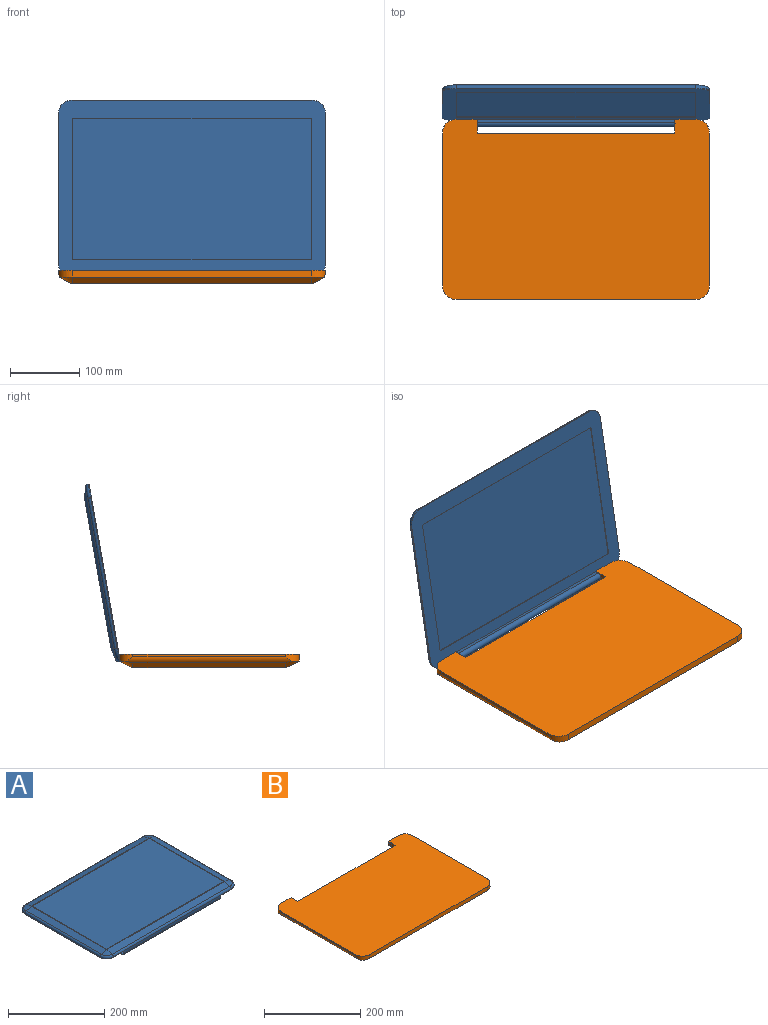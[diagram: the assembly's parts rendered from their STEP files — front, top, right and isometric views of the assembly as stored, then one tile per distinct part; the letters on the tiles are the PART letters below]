
ASSEMBLY  parts=2 mates=1
PART A: 44 faces, bbox 388.3x263.3x20.2 mm
  f0: plane 385x260mm, normal (0,0,-1), area 25707.1mm2, adj f1,f2,f3,f4,f5,f6,f7,f8
  f1: plane 220x1.1mm, normal (1,0,0), area 241.1mm2, adj f0,f2,f8,f22
  f2: cylinder r=20mm len=20mm, axis (0,0,-1), area 34.4mm2, adj f0,f1,f3,f24
  f3: plane 345x1.1mm, normal (0,1,0), area 378.2mm2, adj f0,f2,f4,f25
  f4: cylinder r=20mm len=20mm, axis (0,0,-1), area 34.4mm2, adj f0,f3,f5,f23
  f5: plane 220x1.1mm, normal (-1,0,0), area 241.1mm2, adj f0,f4,f6,f21
  f6: cylinder r=20mm len=20mm, axis (0,0,-1), area 34.4mm2, adj f0,f5,f7,f19
  f7: plane 345x6.3mm, normal (0,-1,0), area 1860.2mm2, adj f0,f6,f8,f18,f39,f41,f42
  f8: cylinder r=20mm len=20mm, axis (0,0,-1), area 34.4mm2, adj f0,f1,f7,f20
  f9: plane 343.77x218.77mm, normal (0,0,1), area 75206mm2, adj f27,f28,f31,f32
  f10: cone r=20mm half-angle=76deg, axis (0,0,-1), area 212.5mm2, adj f11,f12,f24,f26
  f11: plane 345x15.62mm, normal (0,0.24,0.97), area 5553.2mm2, adj f10,f13,f25,f27
  f12: plane 220x15.62mm, normal (0.24,0,0.97), area 3541.1mm2, adj f10,f14,f22,f28
  f13: cone r=20mm half-angle=76deg, axis (0,0,-1), area 212.5mm2, adj f11,f15,f23,f29
  f14: cone r=20mm half-angle=76deg, axis (0,0,-1), area 212.5mm2, adj f12,f16,f20,f30
  f15: plane 220x15.62mm, normal (-0.24,0,0.97), area 3541.1mm2, adj f13,f17,f21,f31
  f16: plane 345x15.62mm, normal (0,-0.24,0.97), area 5553.2mm2, adj f14,f17,f18,f32
  f17: cone r=20mm half-angle=76deg, axis (0,0,-1), area 212.5mm2, adj f15,f16,f19,f33
  f18: cylinder r=5mm len=345mm, axis (1,0,0), area 2287mm2, adj f7,f16,f19,f20
  f19: torus R=15mm, axis (0,0,1), area 194.3mm2, adj f6,f17,f18,f21
  f20: torus R=15mm, axis (0,0,1), area 194.3mm2, adj f8,f14,f18,f22
  f21: cylinder r=5mm len=220mm, axis (0,-1,0), area 1458.4mm2, adj f5,f15,f19,f23
  f22: cylinder r=5mm len=220mm, axis (0,1,0), area 1458.4mm2, adj f1,f12,f20,f24
  f23: torus R=15mm, axis (0,0,1), area 194.3mm2, adj f4,f13,f21,f25
  f24: torus R=15mm, axis (0,0,1), area 194.3mm2, adj f2,f10,f22,f25
  f25: cylinder r=5mm len=345mm, axis (-1,0,0), area 2287mm2, adj f3,f11,f23,f24
  f26: bspline ~1.21x1.21mm, area 0.2mm2, adj f10,f27,f28
  f27: cylinder r=5mm len=345mm, axis (-1,0,0), area 421.8mm2, adj f9,f11,f26,f29
  f28: cylinder r=5mm len=220mm, axis (0,-1,0), area 268.7mm2, adj f9,f12,f26,f30
  f29: bspline ~1.21x1.21mm, area 0.2mm2, adj f13,f27,f31
  f30: bspline ~1.21x1.21mm, area 0.2mm2, adj f14,f28,f32
  f31: cylinder r=5mm len=220mm, axis (0,-1,0), area 268.7mm2, adj f9,f15,f29,f33
  f32: cylinder r=5mm len=345mm, axis (-1,0,0), area 421.8mm2, adj f9,f16,f30,f33
  f33: bspline ~1.21x1.21mm, area 0.2mm2, adj f17,f31,f32
  f34: plane 343.49x1mm, normal (0,-1,0), area 343.5mm2, adj f0,f35,f37,f38
  f35: plane 207.28x1mm, normal (-1,0,0), area 207.3mm2, adj f0,f34,f36,f38
  f36: plane 343.49x1mm, normal (0,1,0), area 343.5mm2, adj f0,f35,f37,f38
  f37: plane 207.28x1mm, normal (1,0,0), area 207.3mm2, adj f0,f34,f36,f38
  f38: plane 343.49x207.28mm, normal (0,0,-1), area 71199.5mm2, adj f34,f35,f36,f37
  f39: plane 10.2x10mm, normal (-1,0,0), area 41mm2, adj f0,f7,f40,f42,f43
  f40: plane 285x5.2mm, normal (0,1,0), area 1482mm2, adj f0,f39,f41,f42
  f41: plane 10.2x10mm, normal (1,0,0), area 41mm2, adj f0,f7,f40,f42,f43
  f42: cylinder r=5mm len=285mm, axis (-1,0,0), area 4476.8mm2, adj f7,f39,f40,f41
  f43: cylinder r=4mm len=285mm, axis (1,0,0), area 7162.8mm2, adj f39,f41
PART B: 42 faces, bbox 385x260x20 mm
  f0: cylinder r=20mm len=20mm, axis (0,0,-1), area 285.3mm2, adj f1,f11,f12,f18,f26
  f1: plane 30x10mm, normal (0,1,0), area 300mm2, adj f0,f2,f12,f16
  f2: plane 20x10mm, normal (-1,0,0), area 149.7mm2, adj f1,f3,f12,f14,f40
  f3: plane 285x10mm, normal (0,1,0), area 2850mm2, adj f2,f4,f12,f15
  f4: plane 20x10mm, normal (1,0,0), area 200mm2, adj f3,f5,f12,f17
  f5: plane 30x10mm, normal (0,1,0), area 300mm2, adj f4,f6,f12,f19
  f6: cylinder r=20mm len=20mm, axis (0,0,-1), area 285.3mm2, adj f5,f7,f12,f21,f27
  f7: plane 220x3.82mm, normal (-1,0,0), area 840.3mm2, adj f6,f8,f12,f27
  f8: cylinder r=20mm len=20mm, axis (0,0,-1), area 285.3mm2, adj f7,f9,f12,f25,f27
  f9: plane 345x10mm, normal (0,-1,0), area 3450mm2, adj f8,f10,f12,f24
  f10: cylinder r=20mm len=20mm, axis (0,0,-1), area 285.3mm2, adj f9,f11,f12,f22,f26
  f11: plane 220x3.82mm, normal (1,0,0), area 840.3mm2, adj f0,f10,f12,f26
  f12: plane 385x260mm, normal (0,0,1), area 94056.6mm2, adj f0,f1,f2,f3,f4,f5,f6,f7
  f13: plane 340.28x215.28mm, normal (0,0,-1), area 66660.3mm2, adj f29,f30,f32,f33,f34,f36,f37,f38
  f14: plane 37.89x17.89mm, normal (-0.45,0,-0.89), area 400mm2, adj f2,f15,f16,f32
  f15: plane 320.78x17.89mm, normal (0,0.45,-0.89), area 6057.8mm2, adj f3,f14,f17,f34
  f16: plane 30x17.89mm, normal (0,0.45,-0.89), area 421.1mm2, adj f1,f14,f18,f30
  f17: plane 37.89x17.89mm, normal (0.45,0,-0.89), area 400mm2, adj f4,f15,f19,f36
  f18: cone r=20mm half-angle=63.4deg, axis (0,0,1), area 321.1mm2, adj f0,f16,f20,f26,f28
  f19: plane 30x17.89mm, normal (0,0.45,-0.89), area 421.1mm2, adj f5,f17,f21,f38
  f20: plane 220x12.36mm, normal (0.45,0,-0.89), area 3040.3mm2, adj f18,f22,f26,f29
  f21: cone r=20mm half-angle=63.4deg, axis (0,0,1), area 321.1mm2, adj f6,f19,f23,f27,f39
  f22: cone r=20mm half-angle=63.4deg, axis (0,0,1), area 321.1mm2, adj f10,f20,f24,f26,f31
  f23: plane 220x12.36mm, normal (-0.45,0,-0.89), area 3040.3mm2, adj f21,f25,f27,f37
  f24: plane 345x17.89mm, normal (0,-0.45,-0.89), area 6900mm2, adj f9,f22,f25,f33
  f25: cone r=20mm half-angle=63.4deg, axis (0,0,1), area 321.1mm2, adj f8,f23,f24,f27,f35
  f26: cylinder r=10mm len=238mm, axis (0,1,0), area 2535.3mm2, adj f0,f10,f11,f18,f20,f22
  f27: cylinder r=10mm len=238mm, axis (0,-1,0), area 2535.3mm2, adj f6,f7,f8,f21,f23,f25
  f28: bspline ~4.47x4.47mm, area 3.2mm2, adj f18,f29,f30
  f29: cylinder r=10mm len=220mm, axis (0,1,0), area 1009.1mm2, adj f13,f20,f28,f31
  f30: cylinder r=10mm len=12.11mm, axis (1,0,0), area 40.3mm2, adj f13,f16,f28,f32
  f31: bspline ~4.47x4.47mm, area 3.2mm2, adj f22,f29,f33
  f32: cylinder r=10mm len=24.47mm, axis (0,1,0), area 92.7mm2, adj f13,f14,f30,f34
  f33: cylinder r=10mm len=345mm, axis (1,0,0), area 1588.6mm2, adj f13,f24,f31,f35
  f34: cylinder r=10mm len=329.72mm, axis (1,0,0), area 1508mm2, adj f13,f15,f32,f36
  f35: bspline ~4.47x4.47mm, area 3.2mm2, adj f25,f33,f37
  f36: cylinder r=10mm len=24.47mm, axis (0,1,0), area 92.7mm2, adj f13,f17,f34,f38
  f37: cylinder r=10mm len=220mm, axis (0,1,0), area 1009.1mm2, adj f13,f23,f35,f39
  f38: cylinder r=10mm len=12.11mm, axis (1,0,0), area 40.3mm2, adj f13,f19,f36,f39
  f39: bspline ~4.47x4.47mm, area 3.6mm2, adj f21,f37,f38
  f40: cylinder r=4mm len=8mm, axis (-1,0,0), area 25.1mm2, adj f2,f41
  f41: plane 8x8mm, normal (-1,0,0), area 50.3mm2, adj f40
PLACE A rot(axis=(0,-0.77,-0.64),180deg) t=(0,160.44,137.2)mm
PLACE B t=(0,9.66,0)mm
MATE revolute B.f40 <-> A.f42  axis (-1,0,0) through (142.5,133.61,15)mm
